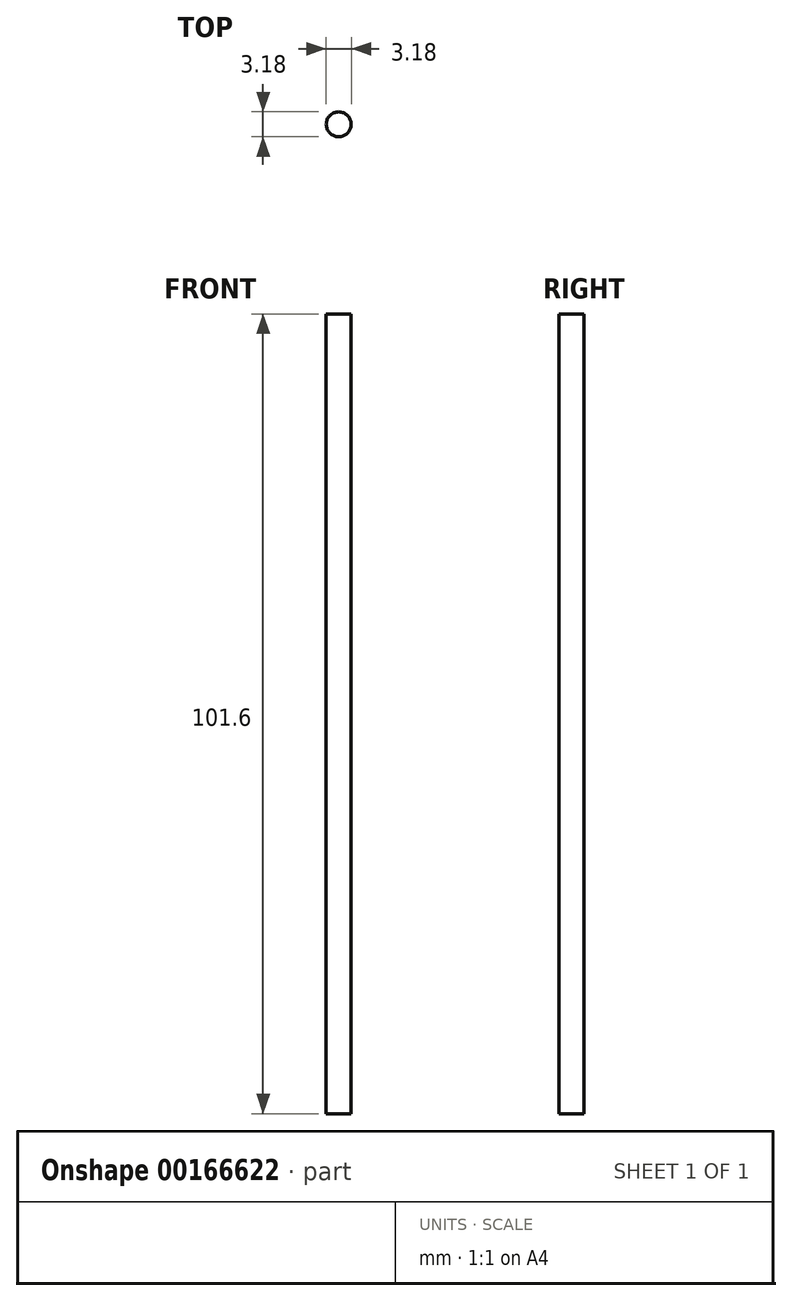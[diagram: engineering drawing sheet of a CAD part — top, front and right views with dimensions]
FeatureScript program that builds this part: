
annotation { "Feature Type Name" : "Feature", "Feature Type Description" : "" }
export const myFeature = defineFeature(function(context is Context, id is Id, definition is map)
    precondition{}
    {
        {
            var Q0;
            Q0=qCreatedBy(makeId("Top.planeOp"),FACE);
            var sketch = newSketch(context, id + "F0", { "sketchPlane" : qUnion([Q0])});
            skCircle(sketch, "E0", {"center": v(0, 0) * mm, "radius": 1.59 * mm});
            skSolve(sketch);
        }
        {
            var Q0;
            Q0=makeQuery(id+"F0.imprint","IMPRINT",FACE,{"disambiguationData":[TD([[makeQuery(id+"F0.imprint","IMPRINT",EDGE,{"derivedFrom":sQuery(id+"F0.wireOp",EDGE,"E0")}),1.0]])]});
            extrude(context, id + "F1", {"entities" : qUnion([Q0]), "depth" : 101.6 * mm});
        }
    });
